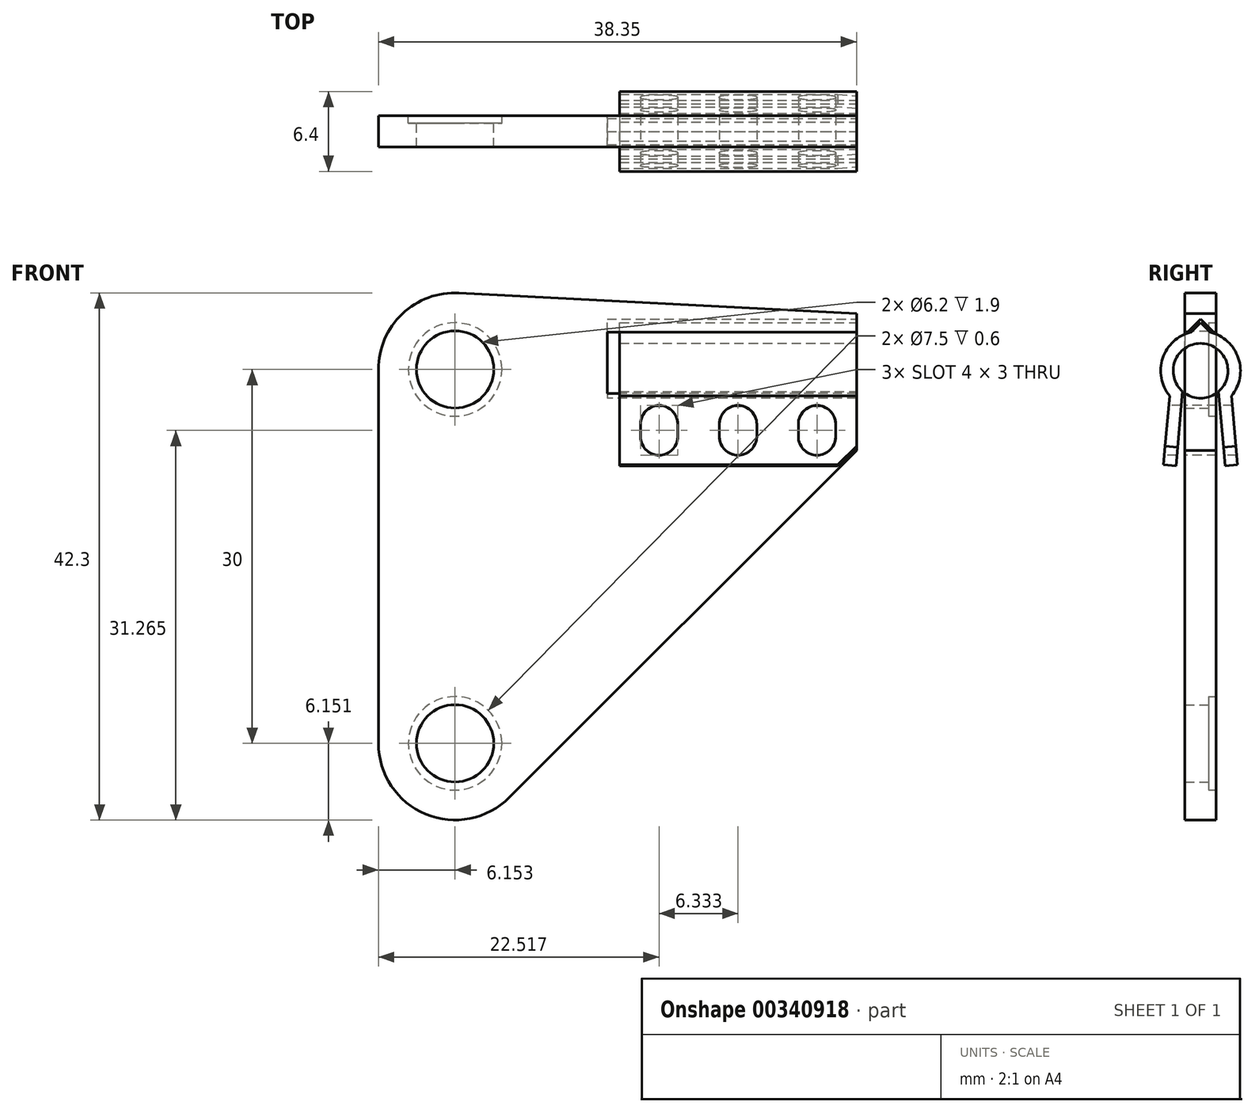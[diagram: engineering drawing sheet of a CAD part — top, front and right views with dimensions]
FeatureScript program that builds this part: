
annotation { "Feature Type Name" : "Feature", "Feature Type Description" : "" }
export const myFeature = defineFeature(function(context is Context, id is Id, definition is map)
    precondition{}
    {
        {
            var Q0;
            Q0=qCreatedBy(makeId("Front.planeOp"),FACE);
            var sketch = newSketch(context, id + "F0", { "sketchPlane" : qUnion([Q0])});
            skCircle(sketch, "E0", {"center": v(-10.32, 13.73) * mm, "radius": 3.15 * mm, "construction": true});
            skCircle(sketch, "E1", {"center": v(-10.32, -16.27) * mm, "radius": 3.15 * mm, "construction": true});
            skLineSegment(sketch, "E2", {"start": v(-16.47, 13.73) * mm, "end": v(-16.47, -16.27) * mm});
            skArc(sketch, "E3", {"start": v(-16.47, 13.73) * mm, "mid": v(-14.55, 18.2) * mm, "end": v(-10, 19.87) * mm});
            skArc(sketch, "E4", {"start": v(-16.47, -16.27) * mm, "mid": v(-12.67, -21.95) * mm, "end": v(-5.97, -20.62) * mm});
            skLineSegment(sketch, "E5", {"start": v(-10, 19.87) * mm, "end": v(21.88, 18.23) * mm});
            skLineSegment(sketch, "E6", {"start": v(21.88, 18.23) * mm, "end": v(21.88, 16.73) * mm});
            skLineSegment(sketch, "E7", {"start": v(21.88, 16.73) * mm, "end": v(1.88, 16.73) * mm});
            skLineSegment(sketch, "E8", {"start": v(1.88, 16.73) * mm, "end": v(1.88, 10.73) * mm});
            skLineSegment(sketch, "E9", {"start": v(1.88, 10.73) * mm, "end": v(21.88, 10.73) * mm});
            skLineSegment(sketch, "E10", {"start": v(21.88, 10.73) * mm, "end": v(21.88, 7.23) * mm});
            skLineSegment(sketch, "E11", {"start": v(-5.97, -20.62) * mm, "end": v(21.88, 7.23) * mm});
            skPoint(sketch, "E12", {"position": v(1.88, 13.73) * mm});
            skSolve(sketch);
        }
        {
            var Q0;
            Q0=makeQuery(id+"F0.imprint","IMPRINT",FACE,{"disambiguationData":[TD([[makeQuery(id+"F0.imprint","IMPRINT",EDGE,{"derivedFrom":sQuery(id+"F0.wireOp",EDGE,"E2")}),1.0]])]});
            extrude(context, id + "F1", {"entities" : qUnion([Q0]), "depth" : 2.5 * mm, "offsetDistance" : 25 * mm});
        }
        {
            var Q0;
            Q0=makeQuery(id+"F1.opExtrude","SWEPT_FACE",FACE,{"disambiguationData":[OSD([sQuery(id+"F0.wireOp",EDGE,"E6")])]});
            var sketch = newSketch(context, id + "F2", { "sketchPlane" : qUnion([Q0])});
            skLineSegment(sketch, "E13", {"start": v(-2.3, 16.73) * mm, "end": v(-1.25, 17.78) * mm});
            skPoint(sketch, "E13.endSnap0", {"position": v(-1.25, 16.73) * mm});
            skLineSegment(sketch, "E14", {"start": v(-1.25, 17.78) * mm, "end": v(-0.2, 16.73) * mm});
            skSolve(sketch);
        }
        {
            var Q0;
            {var subQ0=sQuery(id+"F2.wireOp",EDGE,"E13");Q0=makeQuery(id+"F2.imprint","IMPRINT",FACE,{"disambiguationData":[TD([[makeQuery(id+"F2.imprint","IMPRINT",EDGE,{"derivedFrom":subQ0}),-1.0]])]});}
            var Q1;
            Q1=makeQuery(id+"F1.opExtrude","SWEPT_FACE",FACE,{"disambiguationData":[OSD([sQuery(id+"F0.wireOp",EDGE,"E8")])]});
            extrude(context, id + "F3", {"entities" : qUnion([Q0]), "operationType" : NewBodyOperationType.REMOVE, "endBound" : BoundingType.UP_TO_SURFACE, "oppositeDirection" : true, "depth" : 25 * mm, "endBoundEntityFace" : qUnion([Q1]), "offsetDistance" : 25 * mm});
        }
        {
            var Q0;
            Q0=makeQuery(id+"F1.opExtrude","SWEPT_FACE",FACE,{"disambiguationData":[OSD([sQuery(id+"F0.wireOp",EDGE,"E10")])]});
            cPlane(context, id + "F4", {"entities" : qUnion([Q0]), "cplaneType" : CPlaneType.OFFSET, "offset" : 0 * mm, "width" : 150 * mm, "height" : 150 * mm});
        }
        {
            var Q0;
            Q0=qCreatedBy(id+"F4.planeOp",FACE);
            var sketch = newSketch(context, id + "F5", { "sketchPlane" : qUnion([Q0])});
            skArc(sketch, "E15", {"start": v(0.2, 11.97) * mm, "mid": v(-1.25, 15.82) * mm, "end": v(-2.7, 11.97) * mm});
            skArc(sketch, "E16.trimOffspring", {"start": v(1.24, 11.6) * mm, "mid": v(1.78, 14.64) * mm, "end": v(-0.48, 16.73) * mm});
            skLineSegment(sketch, "E17", {"start": v(-2.02, 16.73) * mm, "end": v(-1.25, 17.5) * mm});
            skLineSegment(sketch, "E18.MirrorCS", {"start": v(-0.48, 16.73) * mm, "end": v(-1.25, 17.5) * mm});
            skLineSegment(sketch, "E19", {"start": v(-2.7, 11.97) * mm, "end": v(-3.22, 6) * mm});
            skLineSegment(sketch, "E20", {"start": v(-3.22, 6) * mm, "end": v(-4.22, 6.08) * mm});
            skLineSegment(sketch, "E21", {"start": v(-4.22, 6.08) * mm, "end": v(-3.74, 11.6) * mm});
            skArc(sketch, "E22.trimOffspring", {"start": v(-2.02, 16.73) * mm, "mid": v(-4.28, 14.64) * mm, "end": v(-3.74, 11.6) * mm});
            skLineSegment(sketch, "E23.MirrorCS", {"start": v(1.72, 6.08) * mm, "end": v(1.24, 11.6) * mm});
            skLineSegment(sketch, "E24.MirrorCS", {"start": v(0.72, 6) * mm, "end": v(1.72, 6.08) * mm});
            skLineSegment(sketch, "E25.MirrorCS", {"start": v(0.2, 11.97) * mm, "end": v(0.72, 6) * mm});
            skSolve(sketch);
        }
        {
            var Q0;
            Q0=makeQuery(id+"F5.imprint","IMPRINT",FACE,{"disambiguationData":[TD([[makeQuery(id+"F5.imprint","IMPRINT",EDGE,{"derivedFrom":sQuery(id+"F5.wireOp",EDGE,"E15")}),-1.0]])]});
            extrude(context, id + "F6", {"entities" : qUnion([Q0]), "oppositeDirection" : true, "depth" : 19 * mm, "offsetDistance" : 25 * mm});
        }
        {
            var Q0;
            {var subQ0=sQuery(id+"F0.wireOp",EDGE,"E8");Q0=makeQuery(id+"F3.boolean.opBoolean","MERGE",FACE,{"derivedFrom":[makeQuery(id+"F1.opExtrude","SWEPT_FACE",FACE,{"disambiguationData":[OSD([subQ0])]}),makeQuery(id+"F3.opExtrude","CAP_FACE",FACE,{"disambiguationData":[OSD([subQ0])],"isStart":false})]});}
            var sketch = newSketch(context, id + "F7", { "sketchPlane" : qUnion([Q0])});
            skLineSegment(sketch, "E26.bottom", {"start": v(-2.5, 10.73) * mm, "end": v(0, 10.73) * mm});
            skLineSegment(sketch, "E26.left", {"start": v(-2.5, 10.73) * mm, "end": v(-2.5, 11.81) * mm});
            skLineSegment(sketch, "E26.right", {"start": v(0, 10.73) * mm, "end": v(0, 11.81) * mm});
            skArc(sketch, "E27", {"start": v(-2.5, 11.81) * mm, "mid": v(-1.25, 11.42) * mm, "end": v(0, 11.81) * mm});
            skSolve(sketch);
        }
        {
            var Q0;
            Q0=makeQuery(id+"F7.imprint","IMPRINT",FACE,{"disambiguationData":[TD([[makeQuery(id+"F7.imprint","IMPRINT",EDGE,{"derivedFrom":sQuery(id+"F7.wireOp",EDGE,"E26.bottom")}),1.0]])]});
            var Q1;
            Q1=makeQuery(id+"F1.opExtrude","SWEPT_FACE",FACE,{"disambiguationData":[OSD([sQuery(id+"F0.wireOp",EDGE,"E10")])]});
            extrude(context, id + "F8", {"entities" : qUnion([Q0]), "operationType" : NewBodyOperationType.ADD, "endBound" : BoundingType.UP_TO_SURFACE, "depth" : 19.35 * mm, "endBoundEntityFace" : qUnion([Q1]), "offsetDistance" : 25 * mm});
        }
        {
            var Q0;
            Q0=makeQuery(id+"F1.opExtrude","CAP_FACE",FACE,{"disambiguationData":[OSD([sQuery(id+"F0.wireOp",EDGE,"E0"),sQuery(id+"F0.wireOp",EDGE,"E1"),sQuery(id+"F0.wireOp",EDGE,"E2"),sQuery(id+"F0.wireOp",EDGE,"E3"),sQuery(id+"F0.wireOp",EDGE,"E4"),sQuery(id+"F0.wireOp",EDGE,"E5"),sQuery(id+"F0.wireOp",EDGE,"E6"),sQuery(id+"F0.wireOp",EDGE,"E7"),sQuery(id+"F0.wireOp",EDGE,"E8"),sQuery(id+"F0.wireOp",EDGE,"E9"),sQuery(id+"F0.wireOp",EDGE,"E10"),sQuery(id+"F0.wireOp",EDGE,"E11")])],"isStart":false});
            cPlane(context, id + "F9", {"entities" : qUnion([Q0]), "cplaneType" : CPlaneType.OFFSET, "offset" : 5 * mm, "width" : 150 * mm, "height" : 150 * mm});
        }
        {
            var Q0;
            Q0=qCreatedBy(id+"F9.planeOp",FACE);
            var sketch = newSketch(context, id + "F10", { "sketchPlane" : qUnion([Q0])});
            skPoint(sketch, "E28", {"position": v(6.05, 8.84) * mm});
            skPoint(sketch, "E29", {"position": v(12.38, 8.84) * mm});
            skPoint(sketch, "E30", {"position": v(18.71, 8.84) * mm});
            skPoint(sketch, "E31", {"position": v(9.21, 8.84) * mm});
            skLineSegment(sketch, "E32", {"start": v(6.05, 8.84) * mm, "end": v(2.88, 8.84) * mm, "construction": true});
            skLineSegment(sketch, "E33", {"start": v(18.71, 8.84) * mm, "end": v(21.88, 8.84) * mm, "construction": true});
            skLineSegment(sketch, "E34", {"start": v(6.05, 8.84) * mm, "end": v(9.21, 8.84) * mm, "construction": true});
            skLineSegment(sketch, "E35", {"start": v(12.38, 8.84) * mm, "end": v(9.21, 8.84) * mm, "construction": true});
            skLineSegment(sketch, "E36", {"start": v(12.38, 8.84) * mm, "end": v(15.55, 8.84) * mm, "construction": true});
            skLineSegment(sketch, "E37", {"start": v(15.55, 8.84) * mm, "end": v(18.71, 8.84) * mm, "construction": true});
            skLineSegment(sketch, "E38.bottom", {"start": v(7.55, 6.84) * mm, "end": v(4.55, 6.84) * mm});
            skLineSegment(sketch, "E38.top", {"start": v(7.55, 10.84) * mm, "end": v(4.55, 10.84) * mm});
            skLineSegment(sketch, "E38.left", {"start": v(7.55, 6.84) * mm, "end": v(7.55, 10.84) * mm});
            skLineSegment(sketch, "E38.right", {"start": v(4.55, 6.84) * mm, "end": v(4.55, 10.84) * mm});
            skLineSegment(sketch, "E39.bottom", {"start": v(13.88, 6.84) * mm, "end": v(10.88, 6.84) * mm});
            skLineSegment(sketch, "E39.top", {"start": v(13.88, 10.84) * mm, "end": v(10.88, 10.84) * mm});
            skLineSegment(sketch, "E39.left", {"start": v(13.88, 6.84) * mm, "end": v(13.88, 10.84) * mm});
            skLineSegment(sketch, "E39.right", {"start": v(10.88, 6.84) * mm, "end": v(10.88, 10.84) * mm});
            skLineSegment(sketch, "E40.bottom", {"start": v(20.21, 6.84) * mm, "end": v(17.21, 6.84) * mm});
            skLineSegment(sketch, "E40.top", {"start": v(20.21, 10.84) * mm, "end": v(17.21, 10.84) * mm});
            skLineSegment(sketch, "E40.left", {"start": v(20.21, 6.84) * mm, "end": v(20.21, 10.84) * mm});
            skLineSegment(sketch, "E40.right", {"start": v(17.21, 6.84) * mm, "end": v(17.21, 10.84) * mm});
            skArc(sketch, "E41", {"start": v(7.55, 9.34) * mm, "mid": v(6.05, 10.84) * mm, "end": v(4.55, 9.34) * mm});
            skArc(sketch, "E42", {"start": v(4.55, 8.34) * mm, "mid": v(6.05, 6.84) * mm, "end": v(7.55, 8.34) * mm});
            skArc(sketch, "E43", {"start": v(13.88, 9.34) * mm, "mid": v(12.38, 10.84) * mm, "end": v(10.88, 9.34) * mm});
            skArc(sketch, "E44", {"start": v(10.88, 8.34) * mm, "mid": v(12.38, 6.84) * mm, "end": v(13.88, 8.34) * mm});
            skArc(sketch, "E45", {"start": v(20.21, 9.34) * mm, "mid": v(18.71, 10.84) * mm, "end": v(17.21, 9.34) * mm});
            skArc(sketch, "E46", {"start": v(17.21, 8.34) * mm, "mid": v(18.71, 6.84) * mm, "end": v(20.21, 8.34) * mm});
            skSolve(sketch);
        }
        {
            var Q0;
            Q0=sQuery(id+"F10.wireOp",VERTEX,"E32.start");
            var Q1;
            Q1=sQuery(id+"F10.wireOp",VERTEX,"E35.start");
            var Q2;
            Q2=sQuery(id+"F10.wireOp",VERTEX,"E30");
            var Q3;
            Q3=makeQuery(id+"F1.opExtrude","SWEPT_BODY",BODY,{"disambiguationData":[OSD([sQuery(id+"F0.wireOp",EDGE,"E0"),sQuery(id+"F0.wireOp",EDGE,"E1"),sQuery(id+"F0.wireOp",EDGE,"E2"),sQuery(id+"F0.wireOp",EDGE,"E3"),sQuery(id+"F0.wireOp",EDGE,"E4"),sQuery(id+"F0.wireOp",EDGE,"E5"),sQuery(id+"F0.wireOp",EDGE,"E6"),sQuery(id+"F0.wireOp",EDGE,"E7"),sQuery(id+"F0.wireOp",EDGE,"E8"),sQuery(id+"F0.wireOp",EDGE,"E9"),sQuery(id+"F0.wireOp",EDGE,"E10"),sQuery(id+"F0.wireOp",EDGE,"E11")])]});
            hole(context, id + "F11", {"style" : HoleStyle.SIMPLE, "endStyle" : HoleEndStyle.BLIND, "holeDiameter" : 3 * mm, "majorDiameter" : 5 * mm, "holeDepth" : 5 * mm, "isTappedThrough" : true, "tappedDepth" : 12 * mm, "tapClearance" : 3, "locations" : qUnion([Q0, Q1, Q2]), "scope" : qUnion([Q3])});
        }
        {
            var Q0;
            {var subQ0=sQuery(id+"F10.wireOp",EDGE,"E41");var subQ6=sQuery(id+"F10.wireOp",EDGE,"E38.left");var subQ7=makeQuery(id+"F10.imprint","INTERSECT",VERTEX,{"derivedFrom":[subQ6,subQ0]});Q0=makeQuery(id+"F10.imprint","IMPRINT",FACE,{"disambiguationData":[TD([[makeQuery(id+"F10.imprint","IMPRINT",EDGE,{"disambiguationData":[TD([[subQ7,1.0]])],"derivedFrom":subQ6}),1.0]])]});}
            var Q1;
            {var subQ0=sQuery(id+"F10.wireOp",EDGE,"E43");var subQ1=sQuery(id+"F10.wireOp",EDGE,"E39.left");var subQ2=makeQuery(id+"F10.imprint","INTERSECT",VERTEX,{"derivedFrom":[subQ1,subQ0]});Q1=makeQuery(id+"F10.imprint","IMPRINT",FACE,{"disambiguationData":[TD([[makeQuery(id+"F10.imprint","IMPRINT",EDGE,{"disambiguationData":[TD([[subQ2,1.0]])],"derivedFrom":subQ1}),1.0]])]});}
            var Q2;
            {var subQ0=sQuery(id+"F10.wireOp",EDGE,"E45");var subQ6=sQuery(id+"F10.wireOp",EDGE,"E40.left");var subQ7=makeQuery(id+"F10.imprint","INTERSECT",VERTEX,{"derivedFrom":[subQ6,subQ0]});Q2=makeQuery(id+"F10.imprint","IMPRINT",FACE,{"disambiguationData":[TD([[makeQuery(id+"F10.imprint","IMPRINT",EDGE,{"disambiguationData":[TD([[subQ7,1.0]])],"derivedFrom":subQ6}),1.0]])]});}
            extrude(context, id + "F12", {"entities" : qUnion([Q0, Q1, Q2]), "operationType" : NewBodyOperationType.REMOVE, "oppositeDirection" : true, "depth" : 25 * mm, "offsetDistance" : 25 * mm});
        }
        {
            var Q0;
            Q0=makeQuery(id+"F6.opExtrude","CAP_EDGE",EDGE,{"disambiguationData":[OSD([sQuery(id+"F5.wireOp",EDGE,"E20")])],"isStart":true});
            var Q1;
            Q1=makeQuery(id+"F6.opExtrude","CAP_EDGE",EDGE,{"disambiguationData":[OSD([sQuery(id+"F5.wireOp",EDGE,"E24.MirrorCS")])],"isStart":true});
            chamfer(context, id + "F13", {"entities" : qUnion([Q0, Q1]), "width" : 1.5 * mm, "tangentPropagation" : true});
        }
        {
            var Q0;
            Q0=sQuery(id+"F0.wireOp",VERTEX,"E0.center");
            var Q1;
            Q1=sQuery(id+"F0.wireOp",VERTEX,"E1.center");
            var Q2;
            Q2=makeQuery(id+"F1.opExtrude","SWEPT_BODY",BODY,{"disambiguationData":[OSD([sQuery(id+"F0.wireOp",EDGE,"E2"),sQuery(id+"F0.wireOp",EDGE,"E3"),sQuery(id+"F0.wireOp",EDGE,"E4"),sQuery(id+"F0.wireOp",EDGE,"E5"),sQuery(id+"F0.wireOp",EDGE,"E6"),sQuery(id+"F0.wireOp",EDGE,"E7"),sQuery(id+"F0.wireOp",EDGE,"E8"),sQuery(id+"F0.wireOp",EDGE,"E9"),sQuery(id+"F0.wireOp",EDGE,"E10"),sQuery(id+"F0.wireOp",EDGE,"E11")])]});
            hole(context, id + "F14", {"style" : HoleStyle.C_BORE, "endStyle" : HoleEndStyle.BLIND, "oppositeDirection" : true, "holeDiameter" : 6.2 * mm, "cBoreDiameter" : 7.5 * mm, "cBoreDepth" : 0.6 * mm, "majorDiameter" : 5 * mm, "holeDepth" : 5 * mm, "isTappedThrough" : true, "tappedDepth" : 12 * mm, "tapClearance" : 3, "locations" : qUnion([Q0, Q1]), "scope" : qUnion([Q2])});
        }
    });
